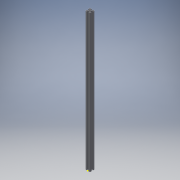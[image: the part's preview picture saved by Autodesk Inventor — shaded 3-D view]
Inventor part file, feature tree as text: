
AUTODESK INVENTOR PART (.ipt)
format: ipt  version: 2017 (Build 210142000, 142)  size: 287,744 bytes
history: native  units: mm
features: sketch x2, other x2, extrude x1, reference x1
ambient origin geometry x8: Origin, YZ Plane, XZ Plane, XY Plane, X Axis, Y Axis, Z Axis, Center Point
bodies: Solid1 (feature_tree)
feature tree (6):
  extrude  "Extrusion1"  [1 undecoded]
  sketch  "Sketch2"
  sketch  "Sketch1"  dims[d0=900.0mm d1=0.0mm]
  reference  "Reference1"
  other  "<userpath>\OneDrive\Inventor\Beast 3D Printer\Assembly3.iam"
  other  "Assembly3.iam"
note: 1 required parameter value undecoded (feature->parameter linkage not recoverable at this tier; creation-order binding heuristic only, values carry confidence <= 0.55)
